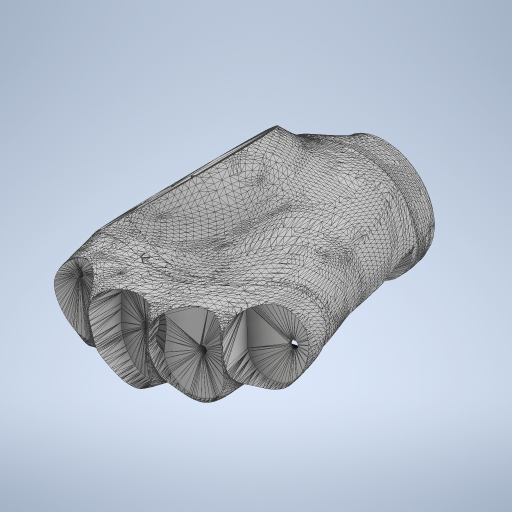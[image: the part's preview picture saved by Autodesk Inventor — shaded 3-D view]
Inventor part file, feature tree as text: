
AUTODESK INVENTOR PART (.ipt)
format: ipt  version: 2024 (Build 280153000, 153)  size: 16,267,264 bytes
history: native  units: in
note: dims shown in document units (in); Inventor stores cm internally (conversion verified against a paired STEP export)
features: extrude x33, sketch x33, other x1
ambient origin geometry x8: Origin, YZ Plane, XZ Plane, XY Plane, X Axis, Y Axis, Z Axis, Center Point
bodies: Solid1 (feature_tree)
feature tree (67):
  other  "Righ_Hand_Palm"
  extrude  "Extrusion1"  Depth=0.0157in TaperAngle=0.0deg
  extrude  "Extrusion2"  Depth=0.0413in TaperAngle=0.0deg
  extrude  "Extrusion3"  Depth=0.0157in TaperAngle=0.0deg
  extrude  "Extrusion4"  Depth=0.0374in TaperAngle=0.0deg
  extrude  "Extrusion5"  Depth=0.3937in TaperAngle=0.0deg
  extrude  "Extrusion6"  Depth=0.0157in TaperAngle=0.0deg
  extrude  "Extrusion8"  Depth=0.0591in TaperAngle=0.0deg
  extrude  "Extrusion9"  Depth=0.0197in TaperAngle=0.0deg
  extrude  "Extrusion10"  Depth=0.4016in TaperAngle=0.0deg
  extrude  "Extrusion11"  Depth=0.3504in TaperAngle=0.0deg
  extrude  "Extrusion13"  Depth=0.1181in TaperAngle=0.0deg
  extrude  "Extrusion14"  Depth=0.0157in TaperAngle=0.0deg
  extrude  "Extrusion15"  Depth=0.002in TaperAngle=0.0deg
  extrude  "Extrusion18"  Depth=0.063in TaperAngle=0.0deg
  extrude  "Extrusion20"  Depth=0.0197in TaperAngle=0.0deg
  extrude  "Extrusion21"  Depth=0.0197in TaperAngle=0.0deg
  extrude  "Extrusion22"  [1 undecoded]
  extrude  "Extrusion23"  [1 undecoded]
  extrude  "Extrusion24"  [1 undecoded]
  extrude  "Extrusion25"  [1 undecoded]
  extrude  "Extrusion26"  [1 undecoded]
  extrude  "Extrusion27"  [1 undecoded]
  extrude  "Extrusion28"  [1 undecoded]
  extrude  "Extrusion29"  [1 undecoded]
  extrude  "Extrusion30"  [1 undecoded]
  extrude  "Extrusion31"  [1 undecoded]
  extrude  "Extrusion32"  [1 undecoded]
  extrude  "Extrusion33"  [1 undecoded]
  extrude  "Extrusion34"  [1 undecoded]
  extrude  "Extrusion36"  [1 undecoded]
  extrude  "Extrusion37"  [1 undecoded]
  extrude  "Extrusion39"  [1 undecoded]
  extrude  "Extrusion40"  [1 undecoded]
  sketch  "Sketch2"  dims[d0=0.0157in d1=0.0in d2=0.0157in d3=0.0in]
  sketch  "Sketch3"  dims[d4=0.0413in d5=0.0in d6=0.1969in d7=0.0in]
  sketch  "Sketch4"  dims[d8=0.0787in d9=0.0in d10=0.0157in d11=0.0in]
  sketch  "Sketch5"  dims[d14=0.0394in d15=0.0in d16=0.0374in d17=0.0in]
  sketch  "Sketch8"  dims[d18=0.0079in d19=0.0in d20=0.3937in d21=0.0in]
  sketch  "Sketch9"  dims[d24=0.3524in d25=0.0in d26=0.0157in d27=0.0in]
  sketch  "Sketch13"  dims[d28=0.1189in d29=0.0in d34=0.0591in d35=0.0in]
  sketch  "Sketch14"  dims[d38=0.0177in d39=0.0in d40=0.0197in d41=0.0in]
  sketch  "Sketch15"  dims[d42=0.4016in d43=0.0in d44=0.3422in d45=0.0in]
  sketch  "Sketch16"  dims[d46=0.4055in d47=0.0in d48=0.3504in d49=0.0in]
  sketch  "Sketch18"  dims[d50=0.002in d51=0.0in d52=0.1181in d53=0.0in]
  sketch  "Sketch20"  dims[d54=0.0394in d55=0.0in d56=0.0157in d57=0.0in]
  sketch  "Sketch22"  dims[d58=0.0157in d59=0.0in d60=0.002in d61=0.0in]
  sketch  "Sketch26"  dims[d62=0.0827in d63=0.0in d64=0.063in d65=0.0in]
  sketch  "Sketch30"  dims[d66=0.1255in d67=0.0in d70=0.0197in d71=0.0in]
  sketch  "Sketch31"  dims[d72=0.2431in d73=0.0in d76=0.0197in d77=0.0in]
  sketch  "Sketch33"  dims[d82=0.0437in d83=0.0in]
  sketch  "Sketch34"
  sketch  "Sketch35"
  sketch  "Sketch36"
  sketch  "Sketch37"
  sketch  "Sketch38"
  sketch  "Sketch41"
  sketch  "Sketch42"
  sketch  "Sketch43"
  sketch  "Sketch44"
  sketch  "Sketch46"
  sketch  "Sketch48"
  sketch  "Sketch49"
  sketch  "Sketch53"
  sketch  "Sketch54"
  sketch  "Sketch56"
  sketch  "Sketch59"
note: 17 required parameter values undecoded (feature->parameter linkage not recoverable at this tier; creation-order binding heuristic only, values carry confidence <= 0.55)
